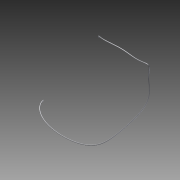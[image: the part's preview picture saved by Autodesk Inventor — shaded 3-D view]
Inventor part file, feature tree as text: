
AUTODESK INVENTOR PART (.ipt)
format: ipt  version: 2012 SP2 (Build 160219200, 219)  size: 178,176 bytes
history: native  units: in
note: dims shown in document units (in); Inventor stores cm internally (conversion verified against a paired STEP export)
features: sketch x2, sweep x1, reference x1
ambient origin geometry x8: Origin, YZ Plane, XZ Plane, XY Plane, X Axis, Y Axis, Z Axis, Center Point
bodies: Solid1 (feature_tree)
feature tree (4):
  sweep  "Sweep1"
  sketch  "Sketch1"  dims[d0=0.0in]
  reference  "Reference1"
  sketch  "3D Sketch1"
